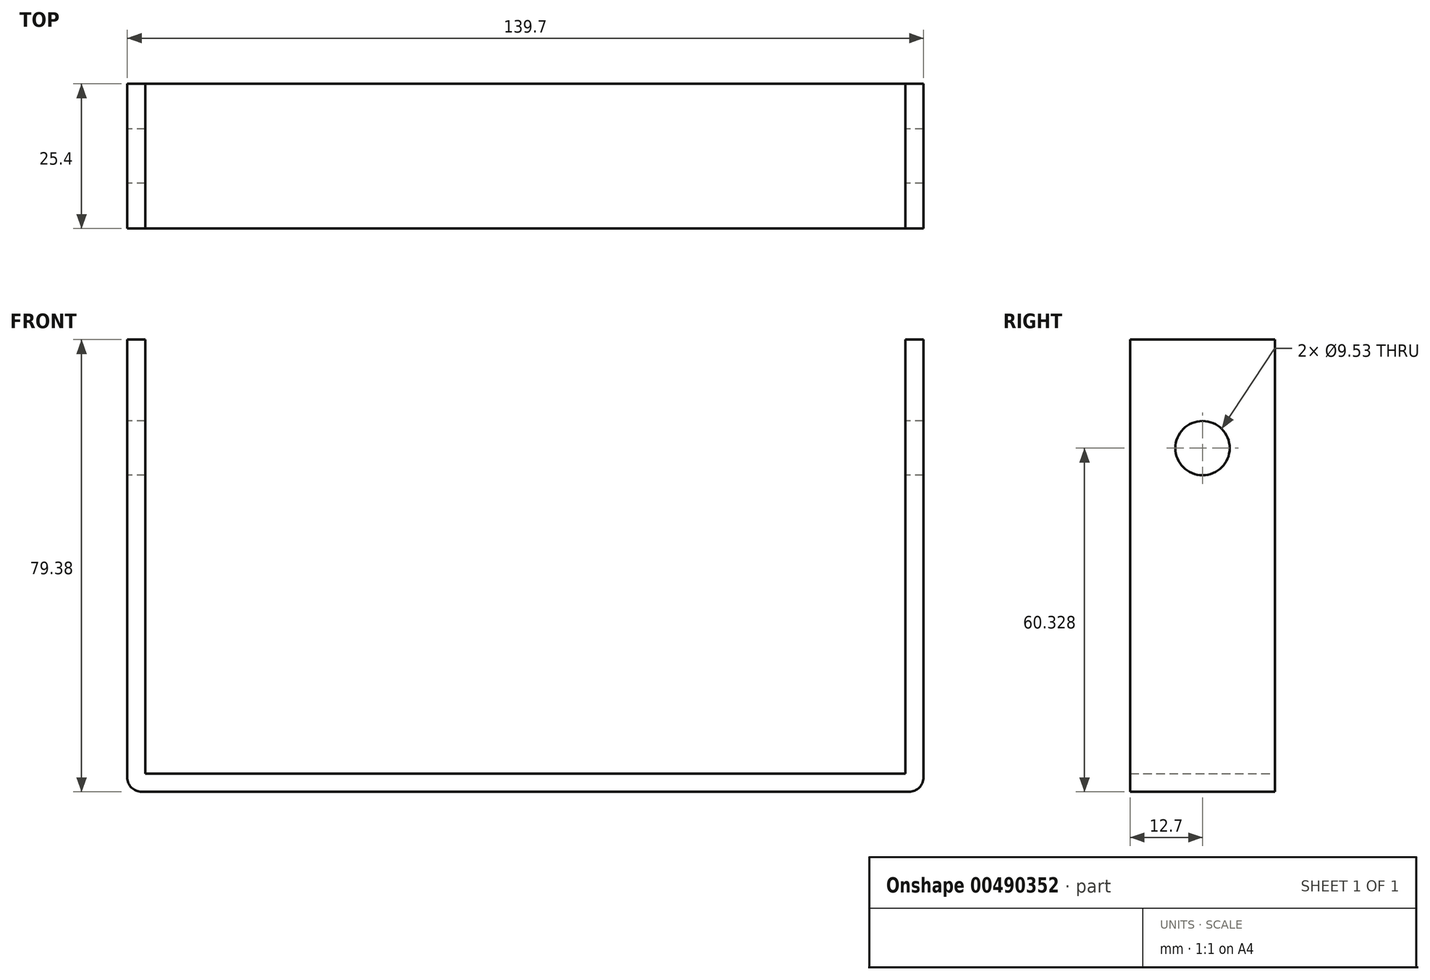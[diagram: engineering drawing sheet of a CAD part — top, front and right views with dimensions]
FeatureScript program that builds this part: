
annotation { "Feature Type Name" : "Feature", "Feature Type Description" : "" }
export const myFeature = defineFeature(function(context is Context, id is Id, definition is map)
    precondition{}
    {
        {
            var Q0;
            Q0=qCreatedBy(makeId("Front.planeOp"),FACE);
            var sketch = newSketch(context, id + "F0", { "sketchPlane" : qUnion([Q0])});
            skLineSegment(sketch, "E0", {"start": v(0, -56.1) * mm, "end": v(-69.85, -56.1) * mm});
            skLineSegment(sketch, "E1", {"start": v(0, -56.1) * mm, "end": v(69.85, -56.1) * mm});
            skLineSegment(sketch, "E2", {"start": v(-69.85, -52.93) * mm, "end": v(-69.85, 23.27) * mm});
            skLineSegment(sketch, "E3", {"start": v(69.85, -52.93) * mm, "end": v(69.85, 23.27) * mm});
            skLineSegment(sketch, "E4", {"start": v(69.85, 23.27) * mm, "end": v(66.68, 23.27) * mm});
            skLineSegment(sketch, "E5", {"start": v(66.68, 23.27) * mm, "end": v(66.68, -52.93) * mm});
            skLineSegment(sketch, "E6", {"start": v(-69.85, 23.27) * mm, "end": v(-66.68, 23.27) * mm});
            skLineSegment(sketch, "E7", {"start": v(-66.68, 23.27) * mm, "end": v(-66.68, -52.93) * mm});
            skLineSegment(sketch, "E8", {"start": v(-69.85, -52.93) * mm, "end": v(-69.85, -56.1) * mm});
            skLineSegment(sketch, "E9", {"start": v(69.85, -52.93) * mm, "end": v(69.85, -56.1) * mm});
            skLineSegment(sketch, "E10", {"start": v(66.68, -52.93) * mm, "end": v(-66.68, -52.93) * mm});
            skSolve(sketch);
        }
        {
            var Q0;
            Q0=makeQuery(id+"F0.imprint","IMPRINT",FACE,{"disambiguationData":[TD([[makeQuery(id+"F0.imprint","IMPRINT",EDGE,{"derivedFrom":sQuery(id+"F0.wireOp",EDGE,"E0")}),-1.0]])]});
            extrude(context, id + "F1", {"entities" : qUnion([Q0]), "depth" : 25.4 * mm});
        }
        {
            var Q0;
            Q0=makeQuery(id+"F1.opExtrude","SWEPT_EDGE",EDGE,{"disambiguationData":[OSD([sQuery(id+"F0.wireOp",EDGE,"E0"),sQuery(id+"F0.wireOp",EDGE,"E8")])]});
            var Q1;
            Q1=makeQuery(id+"F1.opExtrude","SWEPT_EDGE",EDGE,{"disambiguationData":[OSD([sQuery(id+"F0.wireOp",EDGE,"E1"),sQuery(id+"F0.wireOp",EDGE,"E9")])]});
            fillet(context, id + "F2", {"entities" : qUnion([Q0, Q1]), "radius" : 2.54 * mm, "tangentPropagation" : true, "allowEdgeOverflow" : false});
        }
        {
            var Q0;
            Q0=makeQuery(id+"F1.opExtrude","SWEPT_FACE",FACE,{"disambiguationData":[OSD([sQuery(id+"F0.wireOp",EDGE,"E2"),sQuery(id+"F0.wireOp",EDGE,"E8")])]});
            var sketch = newSketch(context, id + "F3", { "sketchPlane" : qUnion([Q0])});
            skCircle(sketch, "E11", {"center": v(12.7, 4.22) * mm, "radius": 4.76 * mm});
            skSolve(sketch);
        }
        {
            var Q0;
            Q0=makeQuery(id+"F3.imprint","IMPRINT",FACE,{"disambiguationData":[TD([[makeQuery(id+"F3.imprint","IMPRINT",EDGE,{"derivedFrom":sQuery(id+"F3.wireOp",EDGE,"E11")}),1.0]])]});
            extrude(context, id + "F4", {"entities" : qUnion([Q0]), "operationType" : NewBodyOperationType.REMOVE, "oppositeDirection" : true, "depth" : 152.4 * mm});
        }
    });
